# Revit family: Grab_Bar-Grohe-Grandera-40633_Series
name_source: partatom
category: Specialty Equipment
revit_build: Autodesk Revit 2014 (Build: 20130308_1515(x64)
units: mm (PartAtom-declared; Revit-internal decimal feet)

## types (2) — shared parameters
Assembly Code = C1030200
Default Elevation = 35 5/8"
Description = Grandera Bath Grip
Height = 1 25/32"
Installation Type = Wall Mounted
Length = 15 5/32"
Manufacturer = GROHE
Price = Prices may vary. Please consult Manufacturer Representative for most up-to-date price list.
Product Page URL = https://www.grohe.ca
URL = https://www.grohe.ca
Warranty Information = Limited Lifetime Warranty
Width = 3 3/8"

## per-type parameters (varying)
| type | Finish | Material |
| 40633EN0 | Metal-Grohe-EN0-Brushed Nickel | Metal-Grohe-EN0-Brushed Nickel |
| 40633000 | Metal-Grohe-000-Chrome | Metal-Grohe-000-Chrome |

note: column(s) folded — value = type name in every type: Model

## geometry (parser evidence)
native form markers: Sweep x1
no freeform markers — native parametric forms only
